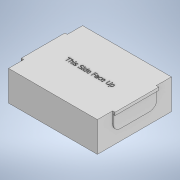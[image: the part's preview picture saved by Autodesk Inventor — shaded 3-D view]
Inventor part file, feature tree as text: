
AUTODESK INVENTOR PART (.ipt)
format: ipt  version: 2020 (Build 240168000, 168)  size: 468,480 bytes
history: native  units: mm
features: extrude x4, sketch x4, projected_geometry x2, fillet x1, mirror x1
ambient origin geometry x8: Origin, YZ Plane, XZ Plane, XY Plane, X Axis, Y Axis, Z Axis, Center Point
bodies: Solid1 (feature_tree)
feature tree (12):
  extrude  "Extrusion1"  Depth=60.96mm
  extrude  "Extrusion2"  Depth=12.7mm
  fillet  "Fillet1"  Radius=30.0mm
  extrude  "Extrusion3"  Depth=5.0mm
  mirror  "Mirror1"
  extrude  "Extrusion4"  Depth=1.17mm TaperAngle=0.0deg
  sketch  "Sketch1"  dims[d0=50.8mm d1=60.96mm]
  sketch  "Sketch2"  dims[d2=20.6629mm d3=0.0mm d4=12.7mm d5=30.0mm]
  projected_geometry  "Projected Loop1"
  sketch  "Sketch3"  dims[d6=0.5mm d7=0.0mm d8=5.0mm]
  projected_geometry  "Projected Loop2"
  sketch  "Sketch4"  dims[d9=2.0mm d10=1.17mm d11=0.0mm d12=1.0mm d13=0.0mm]
